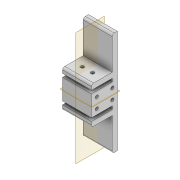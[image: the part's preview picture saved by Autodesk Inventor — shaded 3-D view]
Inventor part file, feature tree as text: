
AUTODESK INVENTOR PART (.ipt)
format: ipt  version: 2022 (Build 260153000, 153)  size: 173,568 bytes
history: native  units: mm
features: extrude x4, sketch x4, plane x2, projected_geometry x2, fillet x1
ambient origin geometry x8: Origin, YZ Plane, XZ Plane, XY Plane, X Axis, Y Axis, Z Axis, Center Point
bodies: Solid1 (feature_tree)
feature tree (13):
  extrude  "Extrusion1"  Depth=100.0mm
  extrude  "Extrusion2"  Depth=5.0mm
  extrude  "Extrusion3"  Depth=10.0mm
  plane  "Work Plane1"
  extrude  "Extrusion11"  Depth=5.0mm
  fillet  "Fillet1"  Radius=3.1mm
  plane  "Work Plane3"
  sketch  "Sketch1"  dims[d0=28.0mm d1=100.0mm]
  sketch  "Sketch3"  dims[d2=5.0mm d3=0.0mm d6=50.0mm]
  projected_geometry  "Projected Loop2"
  sketch  "Sketch4"  dims[d7=100.0mm d8=10.0mm]
  projected_geometry  "Projected Loop3"
  sketch  "Sketch13"  dims[d9=10.0mm d10=5.0mm d11=3.1mm d12=3.1mm d13=5.0mm d14=20.0mm d15=0.0mm d16=3.2mm d17=3.2mm d18=4.95mm d19=4.95mm d20=10.0mm d21=10.0mm d22=100.0mm d23=0.0mm d57=3.0mm d58=3.0mm d59=3.0mm d60=3.0mm d61=5.0mm d62=5.0mm d63=5.0mm d64=5.0mm d65=5.0mm d67=5.0mm d69=5.0mm d70=5.0mm d71=180.0mm d72=0.0mm d73=2.0mm]
